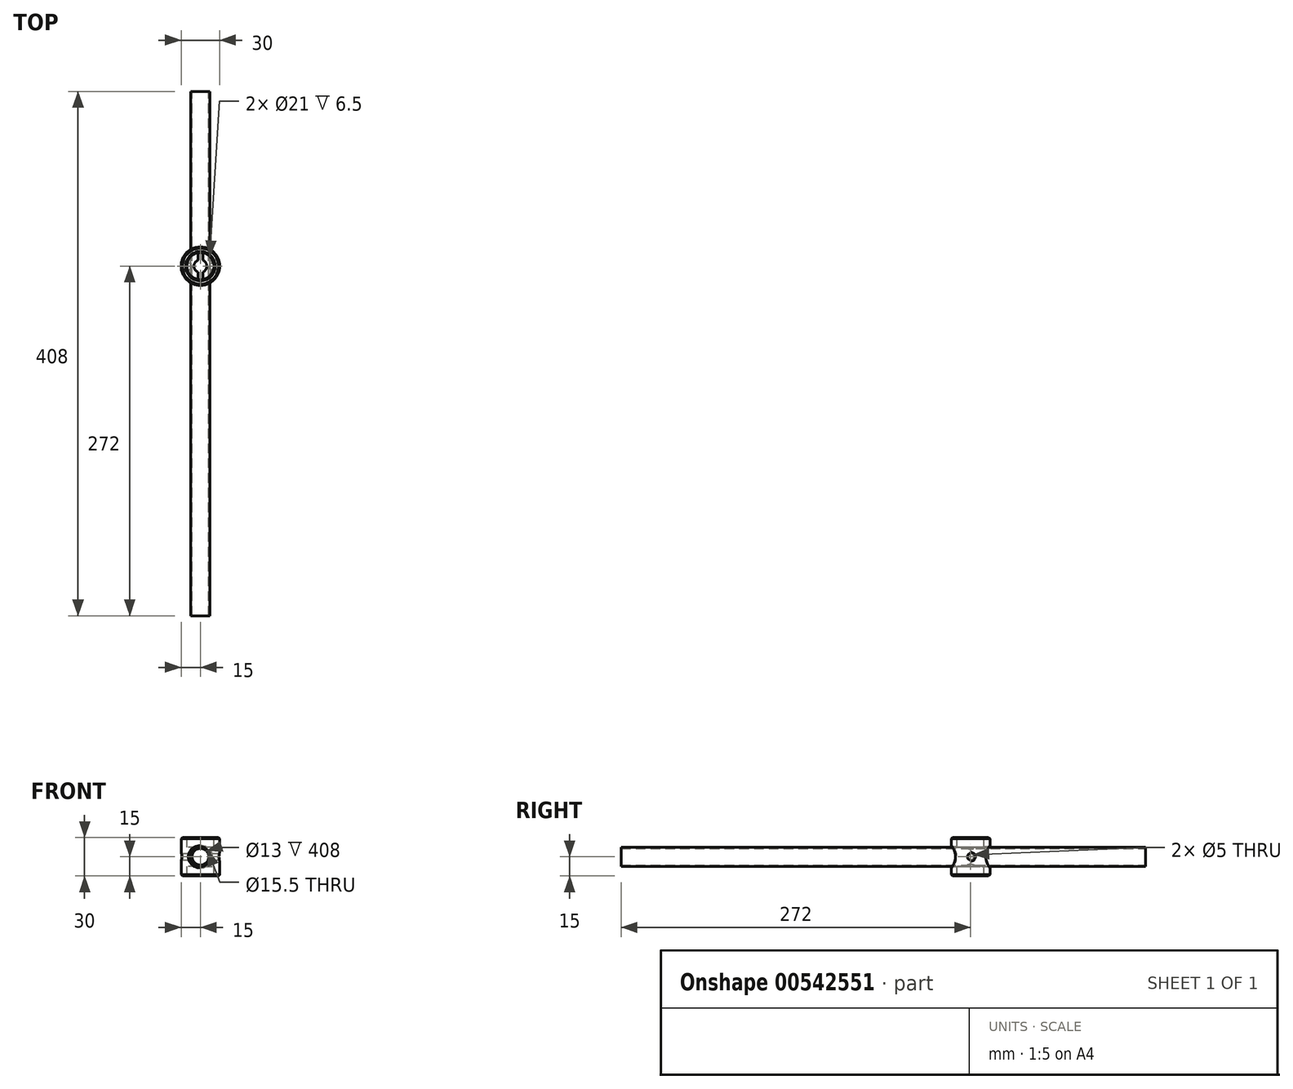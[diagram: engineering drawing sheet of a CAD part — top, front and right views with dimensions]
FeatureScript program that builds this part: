
annotation { "Feature Type Name" : "Feature", "Feature Type Description" : "" }
export const myFeature = defineFeature(function(context is Context, id is Id, definition is map)
    precondition{}
    {
        {
            var Q0;
            Q0=qCreatedBy(makeId("Top.planeOp"),FACE);
            var sketch = newSketch(context, id + "F0", { "sketchPlane" : qUnion([Q0])});
            skCircle(sketch, "E0", {"center": v(0, 0) * mm, "radius": 5 * mm});
            skCircle(sketch, "E1", {"center": v(0, 0) * mm, "radius": 10.5 * mm});
            skLineSegment(sketch, "E2.bottom", {"start": v(-15, -15) * mm, "end": v(15, -15) * mm});
            skLineSegment(sketch, "E2.top", {"start": v(-15, 15) * mm, "end": v(15, 15) * mm});
            skLineSegment(sketch, "E2.left", {"start": v(-15, -15) * mm, "end": v(-15, 15) * mm});
            skLineSegment(sketch, "E2.right", {"start": v(15, -15) * mm, "end": v(15, 15) * mm});
            skSolve(sketch);
        }
        {
            var Q0;
            Q0=makeQuery(id+"F0.imprint","IMPRINT",FACE,{"disambiguationData":[TD([[makeQuery(id+"F0.imprint","IMPRINT",EDGE,{"derivedFrom":sQuery(id+"F0.wireOp",EDGE,"E0")}),-1.0]])]});
            var Q1;
            Q1=makeQuery(id+"F0.imprint","IMPRINT",FACE,{"disambiguationData":[TD([[makeQuery(id+"F0.imprint","IMPRINT",EDGE,{"derivedFrom":sQuery(id+"F0.wireOp",EDGE,"E1")}),-1.0]])]});
            extrude(context, id + "F1", {"entities" : qUnion([Q0, Q1]), "oppositeDirection" : true, "depth" : 30 * mm, "offsetDistance" : 25 * mm});
        }
        {
            var Q0;
            Q0=makeQuery(id+"F0.imprint","IMPRINT",FACE,{"disambiguationData":[TD([[makeQuery(id+"F0.imprint","IMPRINT",EDGE,{"derivedFrom":sQuery(id+"F0.wireOp",EDGE,"E0")}),-1.0]])]});
            extrude(context, id + "F2", {"entities" : qUnion([Q0]), "operationType" : NewBodyOperationType.REMOVE, "oppositeDirection" : true, "depth" : 7.5 * mm, "offsetDistance" : 25 * mm});
        }
        {
            var Q0;
            Q0=makeQuery(id+"F1.opExtrude","SWEPT_FACE",FACE,{"disambiguationData":[OSD([sQuery(id+"F0.wireOp",EDGE,"E2.bottom")])]});
            var sketch = newSketch(context, id + "F3", { "sketchPlane" : qUnion([Q0])});
            skCircle(sketch, "E3", {"center": v(0, -15) * mm, "radius": 7.75 * mm});
            skLineSegment(sketch, "E4", {"start": v(-15, 0) * mm, "end": v(15, -30) * mm, "construction": true});
            skLineSegment(sketch, "E5", {"start": v(15, 0) * mm, "end": v(-15, -30) * mm, "construction": true});
            skSolve(sketch);
        }
        {
            var Q0;
            Q0=makeQuery(id+"F3.imprint","IMPRINT",FACE,{"disambiguationData":[TD([[makeQuery(id+"F3.imprint","IMPRINT",EDGE,{"derivedFrom":sQuery(id+"F3.wireOp",EDGE,"E3")}),1.0]])]});
            extrude(context, id + "F4", {"entities" : qUnion([Q0]), "operationType" : NewBodyOperationType.REMOVE, "endBound" : BoundingType.THROUGH_ALL, "oppositeDirection" : true, "depth" : 25 * mm, "offsetDistance" : 25 * mm});
        }
        {
            var Q0;
            Q0=makeQuery(id+"F0.imprint","IMPRINT",FACE,{"disambiguationData":[TD([[makeQuery(id+"F0.imprint","IMPRINT",EDGE,{"derivedFrom":sQuery(id+"F0.wireOp",EDGE,"E0")}),-1.0]])]});
            var Q1;
            Q1=makeQuery(id+"F1.opExtrude","CAP_FACE",FACE,{"disambiguationData":[OSD([sQuery(id+"F0.wireOp",EDGE,"E0"),sQuery(id+"F0.wireOp",EDGE,"E2.bottom"),sQuery(id+"F0.wireOp",EDGE,"E2.top"),sQuery(id+"F0.wireOp",EDGE,"E2.left"),sQuery(id+"F0.wireOp",EDGE,"E2.right")])],"isStart":false});
            extrude(context, id + "F5", {"entities" : qUnion([Q0]), "operationType" : NewBodyOperationType.REMOVE, "endBound" : BoundingType.UP_TO_SURFACE, "oppositeDirection" : true, "depth" : 25 * mm, "endBoundEntityFace" : qUnion([Q1]), "offsetDistance" : 25 * mm, "hasSecondDirection" : true, "secondDirectionOppositeDirection" : true, "secondDirectionDepth" : (30 - 7.5) * mm});
        }
        {
            var Q0;
            Q0=makeQuery(id+"F1.opExtrude","SWEPT_FACE",FACE,{"disambiguationData":[OSD([sQuery(id+"F0.wireOp",EDGE,"E2.right")])]});
            var sketch = newSketch(context, id + "F6", { "sketchPlane" : qUnion([Q0])});
            skLineSegment(sketch, "E6", {"start": v(-15, -30) * mm, "end": v(15, 0) * mm, "construction": true});
            skLineSegment(sketch, "E7", {"start": v(15, 0) * mm, "end": v(15, -30) * mm, "construction": true});
            skLineSegment(sketch, "E8", {"start": v(15, -30) * mm, "end": v(-15, 0) * mm, "construction": true});
            skCircle(sketch, "E9", {"center": v(0, -15) * mm, "radius": 2.5 * mm});
            skSolve(sketch);
        }
        {
            var Q0;
            Q0=makeQuery(id+"F6.imprint","IMPRINT",FACE,{"disambiguationData":[TD([[makeQuery(id+"F6.imprint","IMPRINT",EDGE,{"derivedFrom":sQuery(id+"F6.wireOp",EDGE,"E9")}),1.0]])]});
            extrude(context, id + "F7", {"entities" : qUnion([Q0]), "operationType" : NewBodyOperationType.REMOVE, "endBound" : BoundingType.THROUGH_ALL, "oppositeDirection" : true, "depth" : 25 * mm, "offsetDistance" : 25 * mm});
        }
        {
            var Q0;
            Q0=qCreatedBy(makeId("Front.planeOp"),FACE);
            var sketch = newSketch(context, id + "F8", { "sketchPlane" : qUnion([Q0])});
            skCircle(sketch, "E10", {"center": v(0, -15) * mm, "radius": 7.5 * mm});
            skCircle(sketch, "E11", {"center": v(0, -15) * mm, "radius": 6.5 * mm});
            skSolve(sketch);
        }
        {
            var Q0;
            Q0 = qSketchRegion(id + "F8", true);
            extrude(context, id + "F9", {"entities" : qUnion([Q0]), "depth" : (13.6 * 20) * mm, "offsetDistance" : 25 * mm, "hasSecondDirection" : true, "secondDirectionOppositeDirection" : true, "secondDirectionDepth" : 13.6 * 10 * mm});
        }
        {
            var Q0;
            Q0=makeQuery(id+"F1.opExtrude","SWEPT_EDGE",EDGE,{"disambiguationData":[OSD([sQuery(id+"F0.wireOp",EDGE,"E2.bottom"),sQuery(id+"F0.wireOp",EDGE,"E2.right")])]});
            var Q1;
            Q1=makeQuery(id+"F1.opExtrude","SWEPT_EDGE",EDGE,{"disambiguationData":[OSD([sQuery(id+"F0.wireOp",EDGE,"E2.top"),sQuery(id+"F0.wireOp",EDGE,"E2.right")])]});
            var Q2;
            Q2=makeQuery(id+"F1.opExtrude","SWEPT_EDGE",EDGE,{"disambiguationData":[OSD([sQuery(id+"F0.wireOp",EDGE,"E2.bottom"),sQuery(id+"F0.wireOp",EDGE,"E2.left")])]});
            var Q3;
            Q3=makeQuery(id+"F1.opExtrude","SWEPT_EDGE",EDGE,{"disambiguationData":[OSD([sQuery(id+"F0.wireOp",EDGE,"E2.top"),sQuery(id+"F0.wireOp",EDGE,"E2.left")])]});
            fillet(context, id + "F10", {"entities" : qUnion([Q0, Q1, Q2, Q3]), "radius" : 15 * mm, "tangentPropagation" : true, "allowEdgeOverflow" : false});
        }
        {
            var Q0;
            Q0=makeQuery(id+"F1.opExtrude","CAP_FACE",FACE,{"disambiguationData":[OSD([sQuery(id+"F0.wireOp",EDGE,"E0"),sQuery(id+"F0.wireOp",EDGE,"E2.bottom"),sQuery(id+"F0.wireOp",EDGE,"E2.top"),sQuery(id+"F0.wireOp",EDGE,"E2.left"),sQuery(id+"F0.wireOp",EDGE,"E2.right")])],"isStart":true});
            var Q1;
            Q1=makeQuery(id+"F1.opExtrude","CAP_FACE",FACE,{"disambiguationData":[OSD([sQuery(id+"F0.wireOp",EDGE,"E0"),sQuery(id+"F0.wireOp",EDGE,"E2.bottom"),sQuery(id+"F0.wireOp",EDGE,"E2.top"),sQuery(id+"F0.wireOp",EDGE,"E2.left"),sQuery(id+"F0.wireOp",EDGE,"E2.right")])],"isStart":false});
            var Q2;
            Q2=makeQuery(id+"F10.opFillet","BLEND_EDGE",EDGE,{"blendedFrom":[makeQuery(id+"F1.opExtrude","SWEPT_EDGE",EDGE,{"disambiguationData":[OSD([sQuery(id+"F0.wireOp",EDGE,"E2.bottom"),sQuery(id+"F0.wireOp",EDGE,"E2.left")])]}),makeQuery(id+"F4.boolean.opBoolean","COPY",FACE,{"derivedFrom":makeQuery(id+"F4.opExtrude","SWEPT_FACE",FACE,{"disambiguationData":[OSD([sQuery(id+"F3.wireOp",EDGE,"E3")])]})})],"blendedInto":[makeQuery(id+"F4.boolean.opBoolean","COPY",FACE,{"derivedFrom":makeQuery(id+"F4.opExtrude","SWEPT_FACE",FACE,{"disambiguationData":[OSD([sQuery(id+"F3.wireOp",EDGE,"E3")])]})})]});
            var Q3;
            Q3=makeQuery(id+"F10.opFillet","BLEND_EDGE",EDGE,{"blendedFrom":[makeQuery(id+"F1.opExtrude","SWEPT_EDGE",EDGE,{"disambiguationData":[OSD([sQuery(id+"F0.wireOp",EDGE,"E2.top"),sQuery(id+"F0.wireOp",EDGE,"E2.left")])]}),makeQuery(id+"F4.boolean.opBoolean","COPY",FACE,{"derivedFrom":makeQuery(id+"F4.opExtrude","SWEPT_FACE",FACE,{"disambiguationData":[OSD([sQuery(id+"F3.wireOp",EDGE,"E3")])]})})],"blendedInto":[makeQuery(id+"F4.boolean.opBoolean","COPY",FACE,{"derivedFrom":makeQuery(id+"F4.opExtrude","SWEPT_FACE",FACE,{"disambiguationData":[OSD([sQuery(id+"F3.wireOp",EDGE,"E3")])]})})]});
            var Q4;
            {var subQ0=sQuery(id+"F0.wireOp",EDGE,"E2.left");Q4=makeQuery(id+"F10.opFillet","BLEND_EDGE",EDGE,{"blendedFrom":[makeQuery(id+"F1.opExtrude","SWEPT_EDGE",EDGE,{"disambiguationData":[OSD([sQuery(id+"F0.wireOp",EDGE,"E2.top"),subQ0])]}),makeQuery(id+"F7.boolean.opBoolean","COPY",FACE,{"disambiguationData":[TD([makeQuery(id+"F1.opExtrude","SWEPT_FACE",FACE,{"disambiguationData":[OSD([subQ0])]})])],"derivedFrom":makeQuery(id+"F7.opExtrude","SWEPT_FACE",FACE,{"disambiguationData":[OSD([sQuery(id+"F6.wireOp",EDGE,"E9")])]})})],"blendedInto":[makeQuery(id+"F7.boolean.opBoolean","COPY",FACE,{"disambiguationData":[TD([makeQuery(id+"F1.opExtrude","SWEPT_FACE",FACE,{"disambiguationData":[OSD([subQ0])]})])],"derivedFrom":makeQuery(id+"F7.opExtrude","SWEPT_FACE",FACE,{"disambiguationData":[OSD([sQuery(id+"F6.wireOp",EDGE,"E9")])]})})]});}
            var Q5;
            {var subQ0=sQuery(id+"F0.wireOp",EDGE,"E2.right");Q5=makeQuery(id+"F10.opFillet","BLEND_EDGE",EDGE,{"blendedFrom":[makeQuery(id+"F1.opExtrude","SWEPT_EDGE",EDGE,{"disambiguationData":[OSD([sQuery(id+"F0.wireOp",EDGE,"E2.top"),subQ0])]}),makeQuery(id+"F7.boolean.opBoolean","COPY",FACE,{"disambiguationData":[TD([makeQuery(id+"F1.opExtrude","SWEPT_FACE",FACE,{"disambiguationData":[OSD([subQ0])]})])],"derivedFrom":makeQuery(id+"F7.opExtrude","SWEPT_FACE",FACE,{"disambiguationData":[OSD([sQuery(id+"F6.wireOp",EDGE,"E9")])]})})],"blendedInto":[makeQuery(id+"F7.boolean.opBoolean","COPY",FACE,{"disambiguationData":[TD([makeQuery(id+"F1.opExtrude","SWEPT_FACE",FACE,{"disambiguationData":[OSD([subQ0])]})])],"derivedFrom":makeQuery(id+"F7.opExtrude","SWEPT_FACE",FACE,{"disambiguationData":[OSD([sQuery(id+"F6.wireOp",EDGE,"E9")])]})})]});}
            chamfer(context, id + "F11", {"entities" : qUnion([Q0, Q1, Q2, Q3, Q4, Q5]), "width" : 1 * mm, "tangentPropagation" : true});
        }
    });
